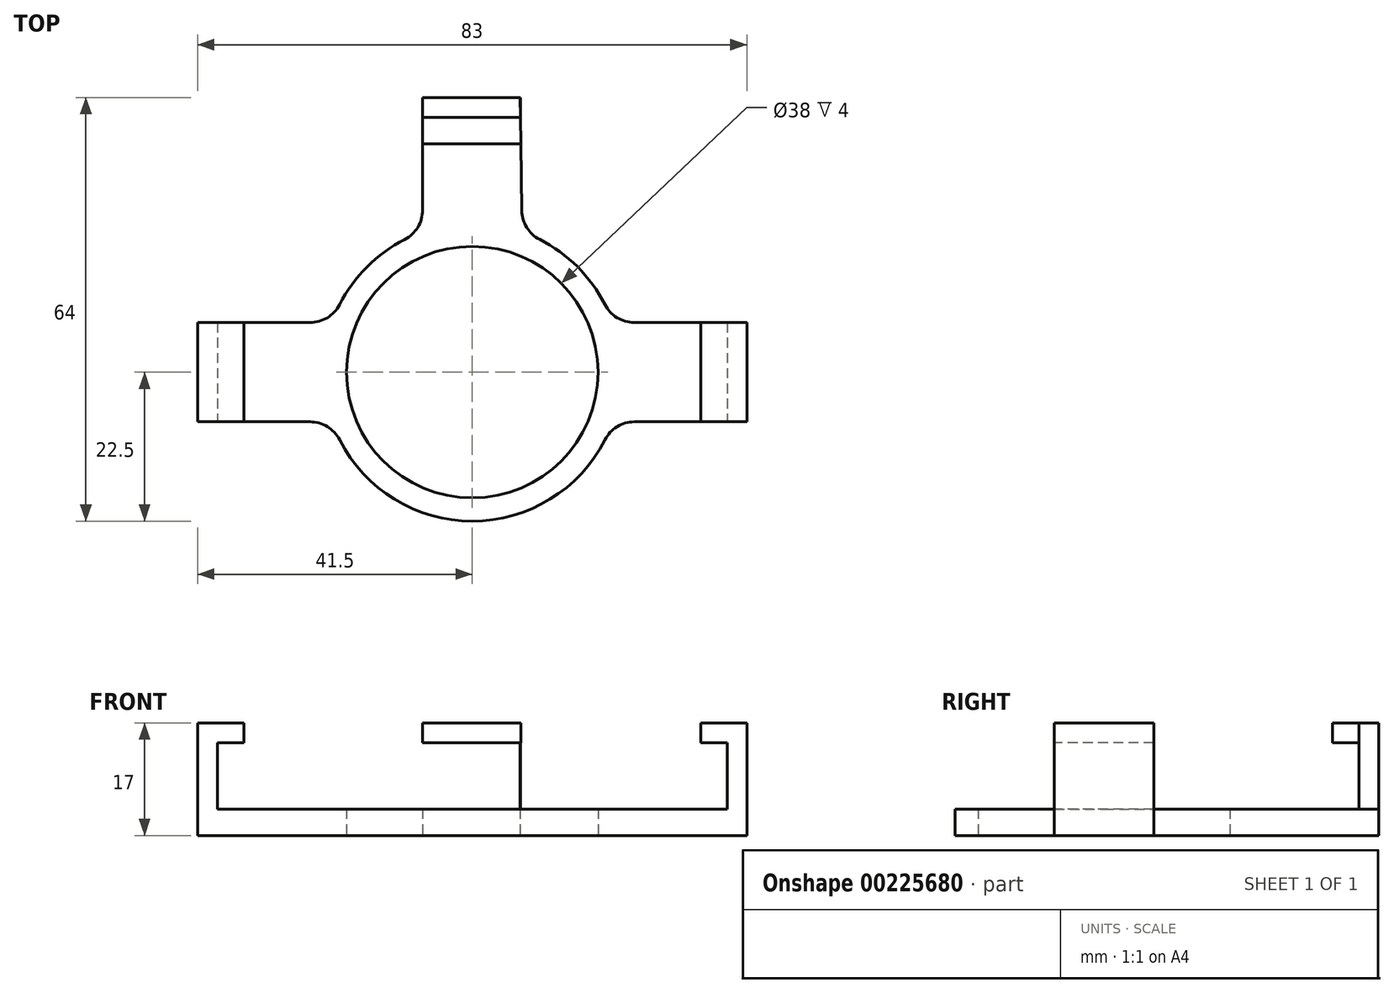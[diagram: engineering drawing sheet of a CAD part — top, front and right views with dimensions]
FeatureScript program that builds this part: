
annotation { "Feature Type Name" : "Feature", "Feature Type Description" : "" }
export const myFeature = defineFeature(function(context is Context, id is Id, definition is map)
    precondition{}
    {
        {
            var Q0;
            Q0=qCreatedBy(makeId("Top.planeOp"),FACE);
            var sketch = newSketch(context, id + "F0", { "sketchPlane" : qUnion([Q0])});
            skCircle(sketch, "E0", {"center": v(0, 0) * mm, "radius": 19 * mm});
            skArc(sketch, "E1", {"start": v(-21.21, -7.5) * mm, "mid": v(0, -22.5) * mm, "end": v(21.21, -7.5) * mm});
            skLineSegment(sketch, "E2.bottom", {"start": v(-41.5, 7.5) * mm, "end": v(-21.21, 7.5) * mm});
            skLineSegment(sketch, "E2.top", {"start": v(-41.5, -7.5) * mm, "end": v(-21.21, -7.5) * mm});
            skLineSegment(sketch, "E2.left", {"start": v(-41.5, 7.5) * mm, "end": v(-41.5, -7.5) * mm});
            skLineSegment(sketch, "E2.right", {"start": v(41.5, 7.5) * mm, "end": v(41.5, -7.5) * mm});
            skLineSegment(sketch, "E3.top", {"start": v(-7.5, 41.5) * mm, "end": v(7.24, 41.5) * mm});
            skLineSegment(sketch, "E4.trimOffspring", {"start": v(-7.5, 21.21) * mm, "end": v(-7.5, 41.5) * mm});
            skLineSegment(sketch, "E5.trimOffspring", {"start": v(7.5, 21.21) * mm, "end": v(7.24, 41.5) * mm});
            skLineSegment(sketch, "E6.trimOffspring", {"start": v(21.21, 7.5) * mm, "end": v(41.5, 7.5) * mm});
            skLineSegment(sketch, "E7.trimOffspring", {"start": v(21.21, -7.5) * mm, "end": v(41.5, -7.5) * mm});
            skPoint(sketch, "E8.orphan", {"position": v(7.5, -41.5) * mm});
            skPoint(sketch, "E9.orphan", {"position": v(-7.24, -41.5) * mm});
            skArc(sketch, "E10.trimOffspring", {"start": v(-7.5, 21.21) * mm, "mid": v(-15.9, 15.9) * mm, "end": v(-21.21, 7.5) * mm});
            skArc(sketch, "E11.trimOffspring", {"start": v(21.21, 7.5) * mm, "mid": v(15.9, 15.9) * mm, "end": v(7.5, 21.21) * mm});
            skSolve(sketch);
        }
        {
            var Q0;
            Q0=makeQuery(id+"F0.imprint","IMPRINT",FACE,{"disambiguationData":[TD([[makeQuery(id+"F0.imprint","IMPRINT",EDGE,{"derivedFrom":sQuery(id+"F0.wireOp",EDGE,"E0")}),-1.0]])]});
            extrude(context, id + "F1", {"entities" : qUnion([Q0]), "depth" : 4 * mm});
        }
        {
            var Q0;
            Q0=makeQuery(id+"F1.opExtrude","CAP_FACE",FACE,{"disambiguationData":[OSD([sQuery(id+"F0.wireOp",EDGE,"E0"),sQuery(id+"F0.wireOp",EDGE,"E1"),sQuery(id+"F0.wireOp",EDGE,"E2.bottom"),sQuery(id+"F0.wireOp",EDGE,"E2.top"),sQuery(id+"F0.wireOp",EDGE,"E2.left"),sQuery(id+"F0.wireOp",EDGE,"E2.right"),sQuery(id+"F0.wireOp",EDGE,"E3.top"),sQuery(id+"F0.wireOp",EDGE,"E4.trimOffspring"),sQuery(id+"F0.wireOp",EDGE,"E5.trimOffspring"),sQuery(id+"F0.wireOp",EDGE,"E6.trimOffspring"),sQuery(id+"F0.wireOp",EDGE,"E7.trimOffspring"),sQuery(id+"F0.wireOp",EDGE,"E10.trimOffspring"),sQuery(id+"F0.wireOp",EDGE,"E11.trimOffspring")])],"isStart":false});
            var sketch = newSketch(context, id + "F2", { "sketchPlane" : qUnion([Q0])});
            skLineSegment(sketch, "E12.bottom", {"start": v(-41.5, 7.5) * mm, "end": v(-38.5, 7.5) * mm});
            skLineSegment(sketch, "E12.top", {"start": v(-41.5, -7.5) * mm, "end": v(-38.5, -7.5) * mm});
            skLineSegment(sketch, "E12.left", {"start": v(-41.5, 7.5) * mm, "end": v(-41.5, -7.5) * mm});
            skLineSegment(sketch, "E12.right", {"start": v(-38.5, 7.5) * mm, "end": v(-38.5, -7.5) * mm});
            skLineSegment(sketch, "E13.bottom", {"start": v(41.5, 7.5) * mm, "end": v(38.5, 7.5) * mm});
            skLineSegment(sketch, "E13.top", {"start": v(41.5, -7.5) * mm, "end": v(38.5, -7.5) * mm});
            skLineSegment(sketch, "E13.left", {"start": v(41.5, 7.5) * mm, "end": v(41.5, -7.5) * mm});
            skLineSegment(sketch, "E13.right", {"start": v(38.5, 7.5) * mm, "end": v(38.5, -7.5) * mm});
            skLineSegment(sketch, "E14.bottom", {"start": v(7.24, 41.5) * mm, "end": v(-7.72, 41.5) * mm});
            skLineSegment(sketch, "E15.bottom", {"start": v(-7.72, 41.5) * mm, "end": v(7.28, 41.5) * mm});
            skLineSegment(sketch, "E15.top", {"start": v(-7.72, 38.5) * mm, "end": v(7.28, 38.5) * mm});
            skLineSegment(sketch, "E15.left", {"start": v(-7.72, 41.5) * mm, "end": v(-7.72, 38.5) * mm});
            skLineSegment(sketch, "E15.right", {"start": v(7.28, 41.5) * mm, "end": v(7.28, 38.5) * mm});
            skLineSegment(sketch, "E16.bottom", {"start": v(-7.72, 38.5) * mm, "end": v(7.33, 38.5) * mm});
            skLineSegment(sketch, "E16.top", {"start": v(-7.72, 34.5) * mm, "end": v(7.33, 34.5) * mm});
            skLineSegment(sketch, "E16.left", {"start": v(-7.72, 38.5) * mm, "end": v(-7.72, 34.5) * mm});
            skLineSegment(sketch, "E16.right", {"start": v(7.33, 38.5) * mm, "end": v(7.33, 34.5) * mm});
            skLineSegment(sketch, "E17.bottom", {"start": v(38.5, 7.5) * mm, "end": v(34.5, 7.5) * mm});
            skLineSegment(sketch, "E17.top", {"start": v(38.5, -7.5) * mm, "end": v(34.5, -7.5) * mm});
            skLineSegment(sketch, "E17.right", {"start": v(34.5, 7.5) * mm, "end": v(34.5, -7.5) * mm});
            skLineSegment(sketch, "E18.bottom", {"start": v(-38.5, 7.5) * mm, "end": v(-34.5, 7.5) * mm});
            skLineSegment(sketch, "E18.top", {"start": v(-38.5, -7.5) * mm, "end": v(-34.5, -7.5) * mm});
            skLineSegment(sketch, "E18.right", {"start": v(-34.5, 7.5) * mm, "end": v(-34.5, -7.5) * mm});
            skSolve(sketch);
        }
        {
            var Q0;
            Q0=makeQuery(id+"F2.imprint","IMPRINT",FACE,{"disambiguationData":[TD([[makeQuery(id+"F2.imprint","IMPRINT",EDGE,{"derivedFrom":sQuery(id+"F2.wireOp",EDGE,"E15.bottom")}),-1.0]])]});
            var Q1;
            Q1=makeQuery(id+"F2.imprint","IMPRINT",FACE,{"disambiguationData":[TD([[makeQuery(id+"F2.imprint","IMPRINT",EDGE,{"derivedFrom":sQuery(id+"F2.wireOp",EDGE,"E12.bottom")}),-1.0]])]});
            var Q2;
            Q2=makeQuery(id+"F2.imprint","IMPRINT",FACE,{"disambiguationData":[TD([[makeQuery(id+"F2.imprint","IMPRINT",EDGE,{"derivedFrom":sQuery(id+"F2.wireOp",EDGE,"E13.bottom")}),-1.0]])]});
            var Q3;
            {var subQ0=sQuery(id+"F2.wireOp",EDGE,"E15.bottom");var subQ1=makeQuery(id+"F1.opExtrude","CAP_EDGE",EDGE,{"disambiguationData":[OSD([sQuery(id+"F0.wireOp",EDGE,"E4.trimOffspring")])],"isStart":false});var subQ2=makeQuery(id+"F2.imprint","INTERSECT",VERTEX,{"derivedFrom":[subQ1,subQ0]});Q3=makeQuery(id+"F2.imprint","IMPRINT",FACE,{"disambiguationData":[TD([[makeQuery(id+"F2.imprint","IMPRINT",EDGE,{"disambiguationData":[TD([[subQ2,-1.0]])],"derivedFrom":subQ0}),-1.0]])]});}
            extrude(context, id + "F3", {"entities" : qUnion([Q0, Q1, Q2, Q3]), "operationType" : NewBodyOperationType.ADD, "depth" : 13 * mm});
        }
        {
            var Q0;
            Q0=makeQuery(id+"F2.imprint","IMPRINT",FACE,{"disambiguationData":[TD([[makeQuery(id+"F2.imprint","IMPRINT",EDGE,{"derivedFrom":sQuery(id+"F2.wireOp",EDGE,"E18.bottom")}),-1.0]])]});
            var Q1;
            Q1=makeQuery(id+"F2.imprint","IMPRINT",FACE,{"disambiguationData":[TD([[makeQuery(id+"F2.imprint","IMPRINT",EDGE,{"derivedFrom":sQuery(id+"F2.wireOp",EDGE,"E17.bottom")}),-1.0]])]});
            var Q2;
            {var subQ3=makeQuery(id+"F1.opExtrude","CAP_EDGE",EDGE,{"disambiguationData":[OSD([sQuery(id+"F0.wireOp",EDGE,"E4.trimOffspring")])],"isStart":false});var subQ5=sQuery(id+"F2.wireOp",EDGE,"E16.top");var subQ7=makeQuery(id+"F2.imprint","INTERSECT",VERTEX,{"derivedFrom":[subQ3,subQ5]});Q2=makeQuery(id+"F2.imprint","IMPRINT",FACE,{"disambiguationData":[TD([[makeQuery(id+"F2.imprint","IMPRINT",EDGE,{"disambiguationData":[TD([[subQ7,-1.0]])],"derivedFrom":subQ3}),-1.0]])]});}
            extrude(context, id + "F4", {"entities" : qUnion([Q0, Q1, Q2]), "operationType" : NewBodyOperationType.ADD, "depth" : 13 * mm});
        }
        {
            var Q0;
            Q0=makeQuery(id+"F1.opExtrude","SWEPT_EDGE",EDGE,{"disambiguationData":[OSD([sQuery(id+"F0.wireOp",EDGE,"E1"),sQuery(id+"F0.wireOp",EDGE,"E2.top")])]});
            var Q1;
            Q1=makeQuery(id+"F1.opExtrude","SWEPT_EDGE",EDGE,{"disambiguationData":[OSD([sQuery(id+"F0.wireOp",EDGE,"E1"),sQuery(id+"F0.wireOp",EDGE,"E7.trimOffspring")])]});
            var Q2;
            Q2=makeQuery(id+"F1.opExtrude","SWEPT_EDGE",EDGE,{"disambiguationData":[OSD([sQuery(id+"F0.wireOp",EDGE,"E6.trimOffspring"),sQuery(id+"F0.wireOp",EDGE,"E11.trimOffspring")])]});
            var Q3;
            Q3=makeQuery(id+"F1.opExtrude","SWEPT_EDGE",EDGE,{"disambiguationData":[OSD([sQuery(id+"F0.wireOp",EDGE,"E5.trimOffspring"),sQuery(id+"F0.wireOp",EDGE,"E11.trimOffspring")])]});
            var Q4;
            Q4=makeQuery(id+"F1.opExtrude","SWEPT_EDGE",EDGE,{"disambiguationData":[OSD([sQuery(id+"F0.wireOp",EDGE,"E2.bottom"),sQuery(id+"F0.wireOp",EDGE,"E10.trimOffspring")])]});
            var Q5;
            Q5=makeQuery(id+"F1.opExtrude","SWEPT_EDGE",EDGE,{"disambiguationData":[OSD([sQuery(id+"F0.wireOp",EDGE,"E4.trimOffspring"),sQuery(id+"F0.wireOp",EDGE,"E10.trimOffspring")])]});
            fillet(context, id + "F5", {"entities" : qUnion([Q0, Q1, Q2, Q3, Q4, Q5]), "radius" : 5 * mm, "tangentPropagation" : true, "allowEdgeOverflow" : false});
        }
        {
            var Q0;
            {var subQ3=makeQuery(id+"F1.opExtrude","CAP_EDGE",EDGE,{"disambiguationData":[OSD([sQuery(id+"F0.wireOp",EDGE,"E4.trimOffspring")])],"isStart":false});var subQ5=sQuery(id+"F2.wireOp",EDGE,"E16.top");var subQ7=makeQuery(id+"F2.imprint","INTERSECT",VERTEX,{"derivedFrom":[subQ3,subQ5]});Q0=makeQuery(id+"F2.imprint","IMPRINT",FACE,{"disambiguationData":[TD([[makeQuery(id+"F2.imprint","IMPRINT",EDGE,{"disambiguationData":[TD([[subQ7,-1.0]])],"derivedFrom":subQ3}),-1.0]])]});}
            var Q1;
            Q1=makeQuery(id+"F2.imprint","IMPRINT",FACE,{"disambiguationData":[TD([[makeQuery(id+"F2.imprint","IMPRINT",EDGE,{"derivedFrom":sQuery(id+"F2.wireOp",EDGE,"E18.bottom")}),-1.0]])]});
            var Q2;
            Q2=makeQuery(id+"F2.imprint","IMPRINT",FACE,{"disambiguationData":[TD([[makeQuery(id+"F2.imprint","IMPRINT",EDGE,{"derivedFrom":sQuery(id+"F2.wireOp",EDGE,"E17.bottom")}),-1.0]])]});
            extrude(context, id + "F6", {"entities" : qUnion([Q0, Q1, Q2]), "operationType" : NewBodyOperationType.REMOVE, "depth" : 10 * mm});
        }
    });
